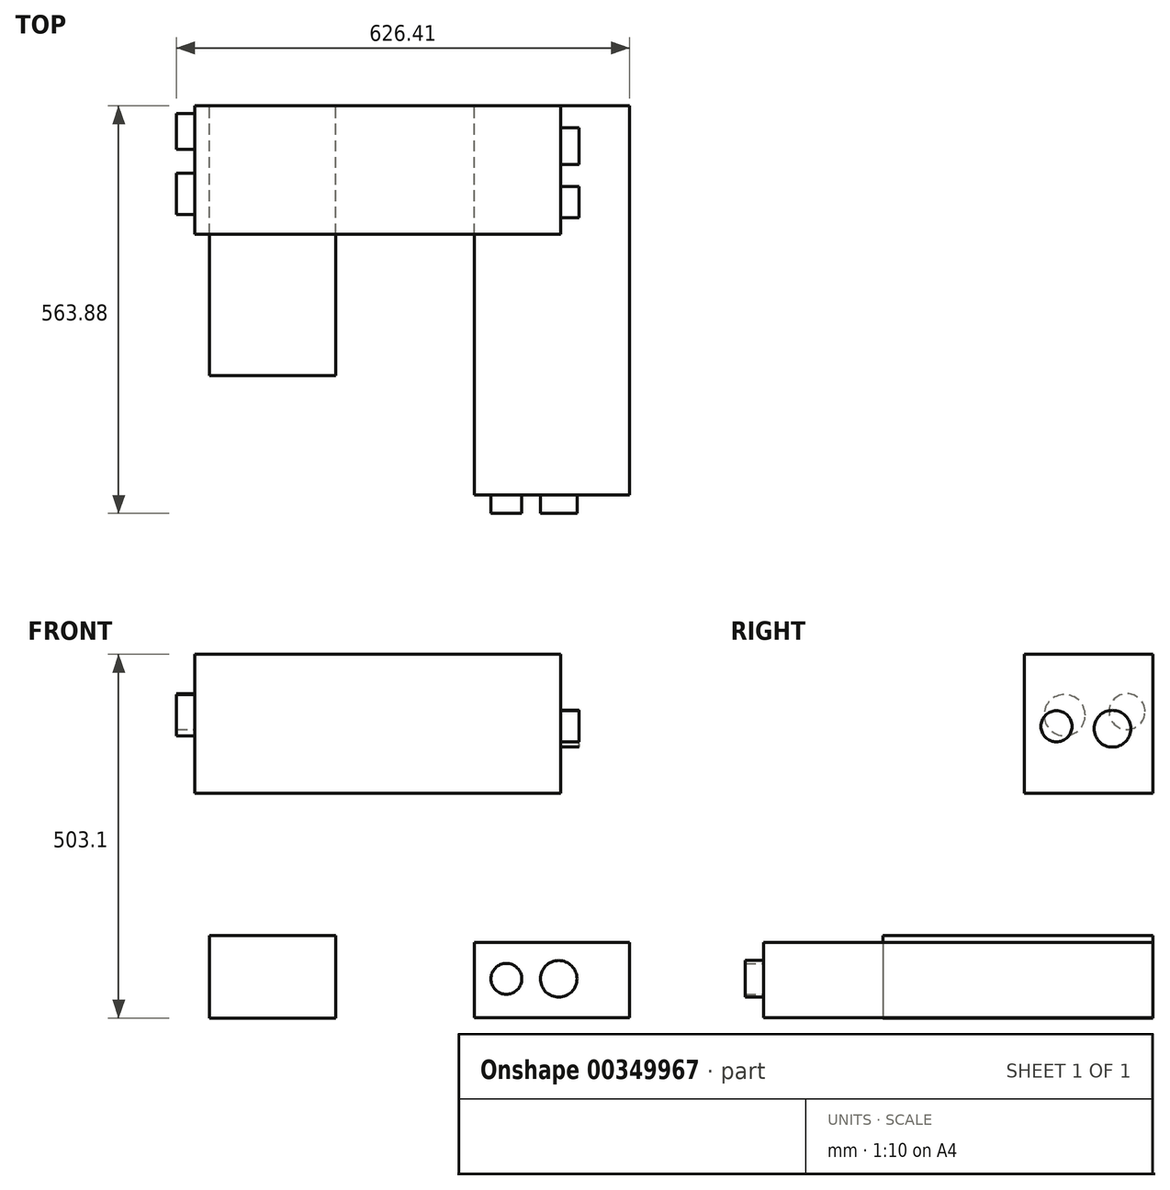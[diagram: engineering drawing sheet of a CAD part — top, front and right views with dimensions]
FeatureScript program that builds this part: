
annotation { "Feature Type Name" : "Feature", "Feature Type Description" : "" }
export const myFeature = defineFeature(function(context is Context, id is Id, definition is map)
    precondition{}
    {
        {
            var Q0;
            Q0=qCreatedBy(makeId("Front.planeOp"),FACE);
            var sketch = newSketch(context, id + "F0", { "sketchPlane" : qUnion([Q0])});
            skLineSegment(sketch, "E0.bottom", {"start": v(-48.15, 43.55) * mm, "end": v(126.47, 43.55) * mm});
            skLineSegment(sketch, "E0.top", {"start": v(-48.15, -70.75) * mm, "end": v(126.47, -70.75) * mm});
            skLineSegment(sketch, "E0.left", {"start": v(-48.15, 43.55) * mm, "end": v(-48.15, -70.75) * mm});
            skLineSegment(sketch, "E0.right", {"start": v(126.47, 43.55) * mm, "end": v(126.47, -70.75) * mm});
            skSolve(sketch);
        }
        {
            var Q0;
            Q0 = qSketchRegion(id + "F0", true);
            extrude(context, id + "F1", {"entities" : qUnion([Q0]), "depth" : 373.08 * mm});
        }
        {
            var Q0;
            Q0=qCreatedBy(makeId("Front.planeOp"),FACE);
            var sketch = newSketch(context, id + "F2", { "sketchPlane" : qUnion([Q0])});
            skLineSegment(sketch, "E1.bottom", {"start": v(318.75, 33.95) * mm, "end": v(532.91, 33.95) * mm});
            skLineSegment(sketch, "E1.top", {"start": v(318.75, -70.12) * mm, "end": v(532.91, -70.12) * mm});
            skLineSegment(sketch, "E1.left", {"start": v(318.75, 33.95) * mm, "end": v(318.75, -70.12) * mm});
            skLineSegment(sketch, "E1.right", {"start": v(532.91, 33.95) * mm, "end": v(532.91, -70.12) * mm});
            skSolve(sketch);
        }
        {
            var Q0;
            Q0 = qSketchRegion(id + "F2", true);
            extrude(context, id + "F3", {"entities" : qUnion([Q0]), "depth" : 538.48 * mm, "offsetDistance" : 25.4 * mm});
        }
        {
            var Q0;
            Q0=makeQuery(id+"F3.opExtrude","CAP_FACE",FACE,{"disambiguationData":[OSD([sQuery(id+"F2.wireOp",EDGE,"E1.bottom"),sQuery(id+"F2.wireOp",EDGE,"E1.top"),sQuery(id+"F2.wireOp",EDGE,"E1.left"),sQuery(id+"F2.wireOp",EDGE,"E1.right")])],"isStart":false});
            var sketch = newSketch(context, id + "F4", { "sketchPlane" : qUnion([Q0])});
            skCircle(sketch, "E2", {"center": v(362.67, -16.63) * mm, "radius": 21.4 * mm});
            skCircle(sketch, "E3", {"center": v(435.09, -16.63) * mm, "radius": 25.33 * mm});
            skSolve(sketch);
        }
        {
            var Q0;
            Q0 = qSketchRegion(id + "F4", true);
            extrude(context, id + "F5", {"entities" : qUnion([Q0]), "operationType" : NewBodyOperationType.ADD, "depth" : 25.4 * mm, "offsetDistance" : 25.4 * mm});
        }
        {
            var Q0;
            Q0=qCreatedBy(makeId("Front.planeOp"),FACE);
            var sketch = newSketch(context, id + "F6", { "sketchPlane" : qUnion([Q0])});
            skLineSegment(sketch, "E4.bottom", {"start": v(437.6, 240.34) * mm, "end": v(-68.1, 240.34) * mm});
            skLineSegment(sketch, "E4.top", {"start": v(437.6, 432.35) * mm, "end": v(-68.1, 432.35) * mm});
            skLineSegment(sketch, "E4.left", {"start": v(437.6, 240.34) * mm, "end": v(437.6, 432.35) * mm});
            skLineSegment(sketch, "E4.right", {"start": v(-68.1, 240.34) * mm, "end": v(-68.1, 432.35) * mm});
            skPoint(sketch, "E4.middle", {"position": v(184.75, 336.35) * mm});
            skSolve(sketch);
        }
        {
            var Q0;
            Q0 = qSketchRegion(id + "F6", true);
            extrude(context, id + "F7", {"entities" : qUnion([Q0]), "depth" : 177.8 * mm, "offsetDistance" : 25.4 * mm});
        }
        {
            var Q0;
            Q0=makeQuery(id+"F7.opExtrude","SWEPT_FACE",FACE,{"disambiguationData":[OSD([sQuery(id+"F6.wireOp",EDGE,"E4.right")])]});
            var sketch = newSketch(context, id + "F8", { "sketchPlane" : qUnion([Q0])});
            skCircle(sketch, "E5", {"center": v(35.57, 353.22) * mm, "radius": 24.79 * mm});
            skCircle(sketch, "E6", {"center": v(121.89, 348.2) * mm, "radius": 28.42 * mm});
            skSolve(sketch);
        }
        {
            var Q0;
            Q0 = qSketchRegion(id + "F8", true);
            extrude(context, id + "F9", {"entities" : qUnion([Q0]), "operationType" : NewBodyOperationType.ADD, "depth" : 25.4 * mm, "offsetDistance" : 25.4 * mm});
        }
        {
            var Q0;
            Q0=makeQuery(id+"F7.opExtrude","SWEPT_FACE",FACE,{"disambiguationData":[OSD([sQuery(id+"F6.wireOp",EDGE,"E4.left")])]});
            var sketch = newSketch(context, id + "F10", { "sketchPlane" : qUnion([Q0])});
            skCircle(sketch, "E7", {"center": v(-133.17, 332.73) * mm, "radius": 21.53 * mm});
            skCircle(sketch, "E8", {"center": v(-55.77, 329.45) * mm, "radius": 25.4 * mm});
            skSolve(sketch);
        }
        {
            var Q0;
            Q0 = qSketchRegion(id + "F10", true);
            extrude(context, id + "F11", {"entities" : qUnion([Q0]), "operationType" : NewBodyOperationType.ADD, "depth" : 25.4 * mm, "offsetDistance" : 25.4 * mm});
        }
    });
